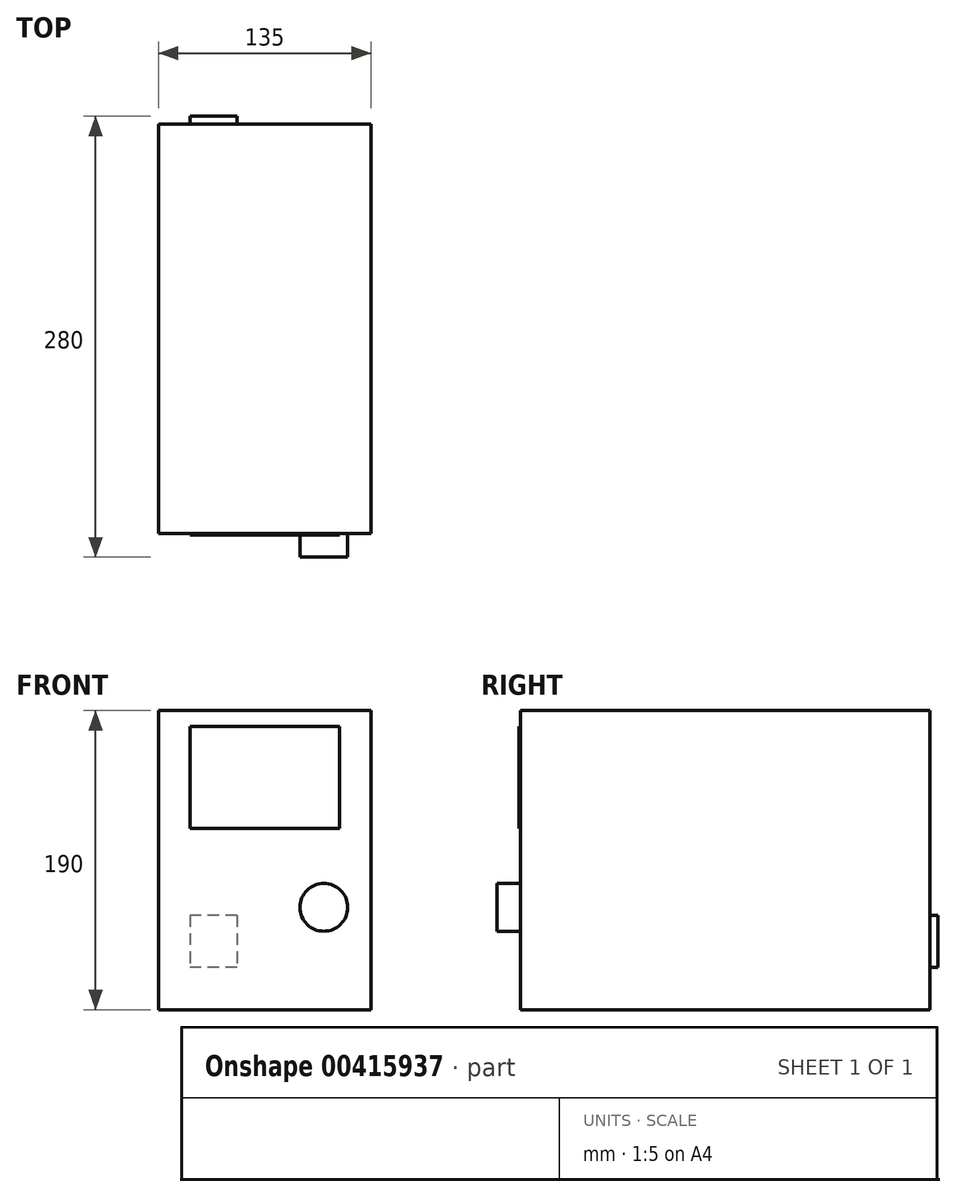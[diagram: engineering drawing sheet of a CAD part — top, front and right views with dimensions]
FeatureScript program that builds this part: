
annotation { "Feature Type Name" : "Feature", "Feature Type Description" : "" }
export const myFeature = defineFeature(function(context is Context, id is Id, definition is map)
    precondition{}
    {
        {
            var Q0;
            Q0=qCreatedBy(makeId("Front.planeOp"),FACE);
            var sketch = newSketch(context, id + "F0", { "sketchPlane" : qUnion([Q0])});
            skLineSegment(sketch, "E0.bottom", {"start": v(-67.5, 95) * mm, "end": v(67.5, 95) * mm});
            skLineSegment(sketch, "E0.top", {"start": v(-67.5, -95) * mm, "end": v(67.5, -95) * mm});
            skLineSegment(sketch, "E0.left", {"start": v(-67.5, 95) * mm, "end": v(-67.5, -95) * mm});
            skLineSegment(sketch, "E0.right", {"start": v(67.5, 95) * mm, "end": v(67.5, -95) * mm});
            skPoint(sketch, "E0.middle", {"position": v(0, 0) * mm});
            skSolve(sketch);
        }
        {
            var Q0;
            Q0=makeQuery(id+"F0.imprint","IMPRINT",FACE,{"disambiguationData":[TD([[makeQuery(id+"F0.imprint","IMPRINT",EDGE,{"derivedFrom":sQuery(id+"F0.wireOp",EDGE,"E0.bottom")}),-1.0]])]});
            extrude(context, id + "F1", {"entities" : qUnion([Q0]), "endBound" : BoundingType.SYMMETRIC, "depth" : 260 * mm});
        }
        {
            var Q0;
            Q0=makeQuery(id+"F1.opExtrude","CAP_FACE",FACE,{"disambiguationData":[OSD([sQuery(id+"F0.wireOp",EDGE,"E0.bottom"),sQuery(id+"F0.wireOp",EDGE,"E0.top"),sQuery(id+"F0.wireOp",EDGE,"E0.left"),sQuery(id+"F0.wireOp",EDGE,"E0.right")])],"isStart":false});
            var sketch = newSketch(context, id + "F2", { "sketchPlane" : qUnion([Q0])});
            skLineSegment(sketch, "E1.bottom", {"start": v(-47.5, 85) * mm, "end": v(47.5, 85) * mm});
            skLineSegment(sketch, "E1.top", {"start": v(-47.5, 20) * mm, "end": v(47.5, 20) * mm});
            skLineSegment(sketch, "E1.left", {"start": v(-47.5, 85) * mm, "end": v(-47.5, 20) * mm});
            skLineSegment(sketch, "E1.right", {"start": v(47.5, 85) * mm, "end": v(47.5, 20) * mm});
            skPoint(sketch, "E2", {"position": v(0, 85) * mm});
            skPoint(sketch, "E3", {"position": v(0, 95) * mm});
            skCircle(sketch, "E4", {"center": v(37.5, -30) * mm, "radius": 15.19 * mm});
            skSolve(sketch);
        }
        {
            var Q0;
            Q0=makeQuery(id+"F2.imprint","IMPRINT",FACE,{"disambiguationData":[TD([[makeQuery(id+"F2.imprint","IMPRINT",EDGE,{"derivedFrom":sQuery(id+"F2.wireOp",EDGE,"E4")}),1.0]])]});
            extrude(context, id + "F3", {"entities" : qUnion([Q0]), "operationType" : NewBodyOperationType.ADD, "depth" : 15 * mm});
        }
        {
            var Q0;
            Q0=makeQuery(id+"F2.imprint","IMPRINT",FACE,{"disambiguationData":[TD([[makeQuery(id+"F2.imprint","IMPRINT",EDGE,{"derivedFrom":sQuery(id+"F2.wireOp",EDGE,"E1.bottom")}),-1.0]])]});
            extrude(context, id + "F4", {"entities" : qUnion([Q0]), "operationType" : NewBodyOperationType.ADD, "depth" : 1 * mm});
        }
        {
            var Q0;
            Q0=makeQuery(id+"F1.opExtrude","CAP_FACE",FACE,{"disambiguationData":[OSD([sQuery(id+"F0.wireOp",EDGE,"E0.bottom"),sQuery(id+"F0.wireOp",EDGE,"E0.top"),sQuery(id+"F0.wireOp",EDGE,"E0.left"),sQuery(id+"F0.wireOp",EDGE,"E0.right")])],"isStart":true});
            var sketch = newSketch(context, id + "F5", { "sketchPlane" : qUnion([Q0])});
            skLineSegment(sketch, "E5.bottom", {"start": v(17.5, -35) * mm, "end": v(47.5, -35) * mm});
            skLineSegment(sketch, "E5.top", {"start": v(17.5, -68) * mm, "end": v(47.5, -68) * mm});
            skLineSegment(sketch, "E5.left", {"start": v(17.5, -35) * mm, "end": v(17.5, -68) * mm});
            skLineSegment(sketch, "E5.right", {"start": v(47.5, -35) * mm, "end": v(47.5, -68) * mm});
            skSolve(sketch);
        }
        {
            var Q0;
            Q0=makeQuery(id+"F5.imprint","IMPRINT",FACE,{"disambiguationData":[TD([[makeQuery(id+"F5.imprint","IMPRINT",EDGE,{"derivedFrom":sQuery(id+"F5.wireOp",EDGE,"E5.bottom")}),-1.0]])]});
            extrude(context, id + "F6", {"entities" : qUnion([Q0]), "operationType" : NewBodyOperationType.ADD, "depth" : 5 * mm});
        }
    });
